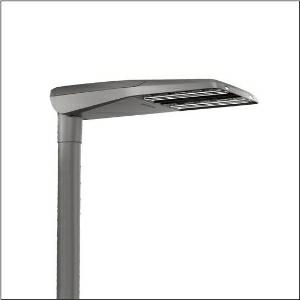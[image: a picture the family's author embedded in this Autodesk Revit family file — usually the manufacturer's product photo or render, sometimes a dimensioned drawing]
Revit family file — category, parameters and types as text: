
# Revit family: streetlight_sl_11_iq_midi___st1_2a_5xc3a21f08me_5047
name_source: partatom
category: Lighting Fixtures
units: mm (PartAtom-declared; Revit-internal decimal feet)

## family parameters
Cut with Voids When Loaded = No
Host = Face
Light Source = No
Part Type = Normal
Room Calculation Point = No
Round Connector Dimension = Use Diameter
Shared = No

## types (1)
- --- (1 x LED, 14840 lm, 124.7 W, 2200K)
    Apparent Load = 125 VA
    CIE Flux Codes = 32 70 96 100 100
    Color Rendering = 70
    Color Temperature = 2200K
    Default Elevation = 1800 mm
    Description = Streetlight SL 11 iQ midi, mast luminaire, primary light control with 3 zone facetted reflector, of plastic, silver coated, highly specular, primary optical cover: cover, of PMMA, transparent, light distribution: ST1.2a, light emission: direct distribution, primary light characteristic: asymmetric, installation type: post-top, side-entry, lamps: LED, High Power LED, rated values: 14.840lm | 124,7W | 119lm/W (begin service life); end service life: 14.840lm | 132,2W; at 50% lumin. flux: 7.420lm | 57,1W | 129,9lm/W, colour temperature: 2200K, colour rendering: CRI > 70, light colour: 722, light setting 1 begin service life: 100% | 14.840lm | 124,7W | 119lm/W | 2.200K, light setting 1 end service life: 132,2W, further light settings possible, control: Street-Remote, optimised constant luminous flux control (CLO 2.0), Desk-Remote (wireless, voltage-free reading and setting of iQ features in the workshop via application-optimized NFC function/RFID function), Light-Fading, Smart-Wire, Night-Set, Lumen-Switch, Temp-Guard, Auto-Match, with cable H07RN-F 3x 1.5mm², mains connection: 230..240V, AC, 50/60Hz, connection cable pre-assembled, cable length: 12,5m, luminaire housing, of diecast aluminium, powder-coated, SITECO metallic grey (DB 702S), please order mast flange separately, inclination adjustable without tools: 0°, 5°, 10°, 15° (post-top) | 0°, -5°, -10°, -15° (side-entry), sealing non-destructively replaceable, multi-level sealing system, length: 780mm, width: 376mm, height: 118mm, mast flange for spigot size: 42mm (side-entry): 5XC10008XM4, 60/48mm (side-entry/post-top): 5XC10108XM2, 76/60mm (side-entry/post-top): 5XC10108XM1, equipment: Power, protection rating (complete): IP66, insulation class (complete): insulation class II (safety insulation), certification: CE, ENEC, ENEC+, VDE, impact resistance: IK10, permissible operating ambient temperature for outdoor applications: -25..+50°C, standard-compliant lighting for roads and squares, Environmental Product Declaration (EPD) tested and certified by an independent institute, packaging unit: 1 piece

Light Distribution: ST1.2a
    Height = 118 mm
    Lamp = 1 x LED
    Lamp Light Flux = 14840 lm
    Lamp Power = 124.7 W
    Lamp count = 1
    Length = 780 mm
    Luminous efficacy = 119 lm/W
    Manufacturer = Siteco
    ModVariant = No
    Model = 5XC3A21F08ME
    Number of Poles = 1
    OnlyDefault = Yes
    Power Factor = 1
    Product Name = Streetlight SL 11 iQ midi | ST1.2a
    Product group = mast luminaire | pylon top
    ProductGroupID = 6100
    Protection Class = Protection class II
    Protection Degree = IP 66
    RLX_Detail_Level = 1
    RLX_Emergency_Light_Flux = 0 lm
    RLX_Emergency_Type = 0
    RLX_Emergency_Type_DB = No
    RlxData = <blob elided: 70961 chars, md5=1f57225a>
    Socket = socket
    Standby Power = 0 W
    System Light Flux = 14841 lm
    System Power = 125 W
    Type Comments = factory setting: luminous flux: 100 % | dim-lin: 254 | 557 mA
    Type Image = l_1005960.jpg
    URL = http://relux.com
    VarID = @adj_129595
    Voltage = 0 V
    Weight = 0.00 kg
    Width = 376 mm

## geometry (parser evidence)
native form markers: Blend x4, Sweep x10
no freeform markers — native parametric forms only
